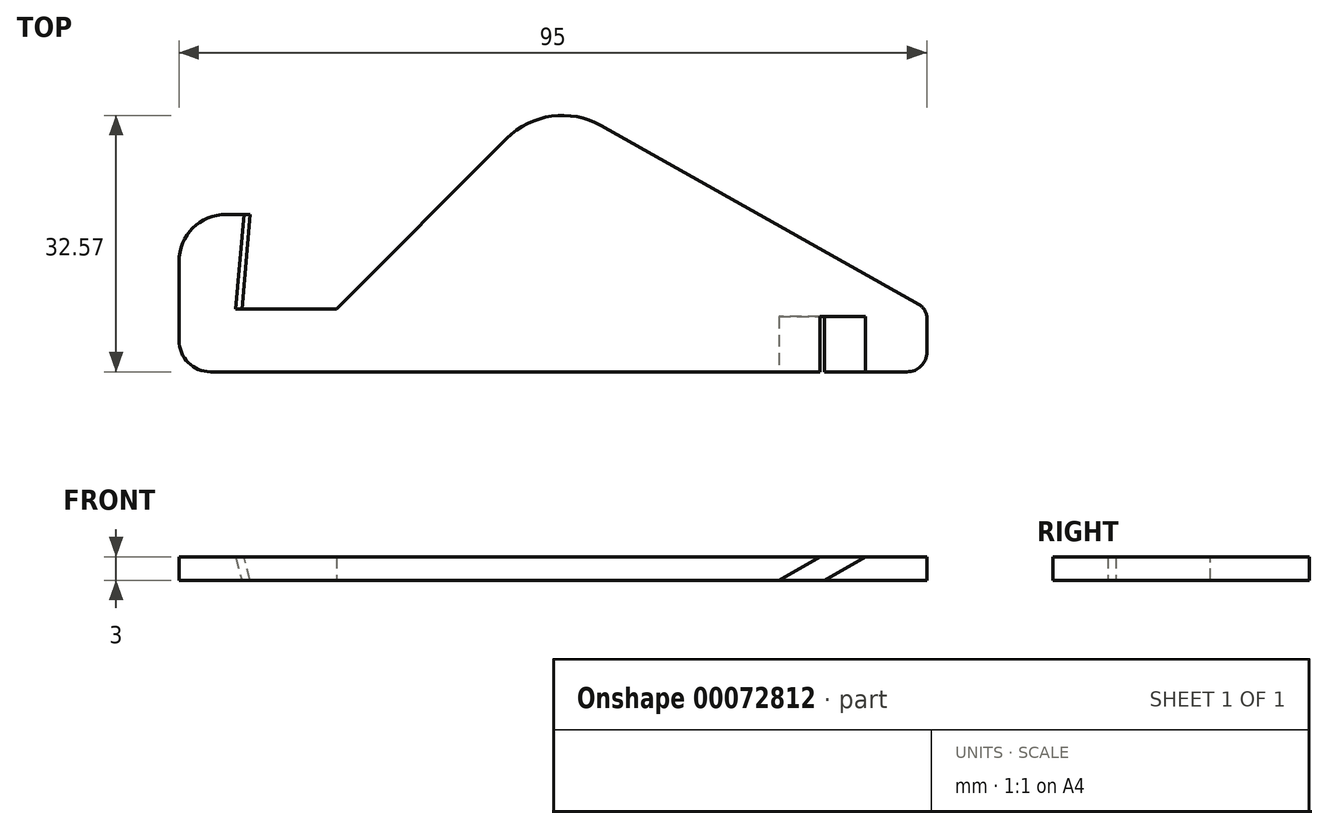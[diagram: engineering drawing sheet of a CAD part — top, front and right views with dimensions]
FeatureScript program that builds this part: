
annotation { "Feature Type Name" : "Feature", "Feature Type Description" : "" }
export const myFeature = defineFeature(function(context is Context, id is Id, definition is map)
    precondition{}
    {
        {
            var Q0;
            Q0=qCreatedBy(makeId("Top.planeOp"),FACE);
            var sketch = newSketch(context, id + "F0", { "sketchPlane" : qUnion([Q0])});
            skLineSegment(sketch, "E0.bottom", {"start": v(0, 0) * mm, "end": v(95, 0) * mm, "construction": true});
            skLineSegment(sketch, "E1", {"start": v(92.5, 0) * mm, "end": v(4, 0) * mm});
            skPoint(sketch, "E2.visualSharp", {"position": v(0, 0) * mm});
            skLineSegment(sketch, "E3", {"start": v(8, 8) * mm, "end": v(20, 8) * mm});
            skLineSegment(sketch, "E4", {"start": v(20, 8) * mm, "end": v(41.64, 29.64) * mm});
            skLineSegment(sketch, "E5", {"start": v(9.05, 20) * mm, "end": v(8, 8) * mm});
            skPoint(sketch, "E6.visualSharp", {"position": v(8, 8) * mm});
            skLineSegment(sketch, "E7", {"start": v(95, 2.5) * mm, "end": v(95, 6.83) * mm});
            skLineSegment(sketch, "E8", {"start": v(93.98, 8.57) * mm, "end": v(53.61, 31.28) * mm});
            skPoint(sketch, "E9.visualSharp", {"position": v(47, 35) * mm});
            skArc(sketch, "E9.filletArc", {"start": v(53.61, 31.28) * mm, "mid": v(47.35, 32.47) * mm, "end": v(41.64, 29.64) * mm});
            skPoint(sketch, "E10.visualSharp", {"position": v(95, 8) * mm});
            skArc(sketch, "E10.filletArc", {"start": v(95, 6.83) * mm, "mid": v(94.73, 7.84) * mm, "end": v(93.98, 8.57) * mm});
            skPoint(sketch, "E11.visualSharp", {"position": v(95, 0) * mm});
            skArc(sketch, "E11.filletArc", {"start": v(92.5, 0) * mm, "mid": v(94.27, 0.73) * mm, "end": v(95, 2.5) * mm});
            skArc(sketch, "E12.filletArc", {"start": v(0, 4) * mm, "mid": v(1.17, 1.17) * mm, "end": v(4, 0) * mm});
            skLineSegment(sketch, "E13", {"start": v(0, 4) * mm, "end": v(0, 14) * mm});
            skLineSegment(sketch, "E14", {"start": v(6, 20) * mm, "end": v(9.05, 20) * mm});
            skPoint(sketch, "E15.visualSharp", {"position": v(0, 20) * mm});
            skArc(sketch, "E15.filletArc", {"start": v(6, 20) * mm, "mid": v(1.76, 18.24) * mm, "end": v(0, 14) * mm});
            skSolve(sketch);
        }
        {
            var Q0;
            Q0=makeQuery(id+"F0.imprint","IMPRINT",FACE,{"disambiguationData":[TD([[makeQuery(id+"F0.imprint","IMPRINT",EDGE,{"derivedFrom":sQuery(id+"F0.wireOp",EDGE,"E1")}),-1.0]])]});
            extrude(context, id + "F1", {"entities" : qUnion([Q0]), "depth" : 3 * mm});
        }
        {
            var Q0;
            Q0=makeQuery(id+"F1.opExtrude","CAP_FACE",FACE,{"disambiguationData":[OSD([sQuery(id+"F0.wireOp",EDGE,"E1"),sQuery(id+"F0.wireOp",EDGE,"E3"),sQuery(id+"F0.wireOp",EDGE,"E4"),sQuery(id+"F0.wireOp",EDGE,"E5"),sQuery(id+"F0.wireOp",EDGE,"E7"),sQuery(id+"F0.wireOp",EDGE,"E8"),sQuery(id+"F0.wireOp",EDGE,"E9.filletArc"),sQuery(id+"F0.wireOp",EDGE,"E10.filletArc"),sQuery(id+"F0.wireOp",EDGE,"E11.filletArc"),sQuery(id+"F0.wireOp",EDGE,"E12.filletArc"),sQuery(id+"F0.wireOp",EDGE,"E13"),sQuery(id+"F0.wireOp",EDGE,"E14"),sQuery(id+"F0.wireOp",EDGE,"E15.filletArc")])],"isStart":true});
            var sketch = newSketch(context, id + "F2", { "sketchPlane" : qUnion([Q0])});
            skLineSegment(sketch, "E16", {"start": v(82, 0) * mm, "end": v(82, -20.57) * mm, "construction": true});
            skSolve(sketch);
        }
        {
            var Q0;
            Q0=sQuery(id+"F2.wireOp",EDGE,"E16");
            cPlane(context, id + "F3", {"entities" : qUnion([Q0]), "cplaneType" : CPlaneType.LINE_ANGLE, "offset" : 150 * mm, "angle" : 60 * degree, "width" : 150 * mm, "height" : 150 * mm});
        }
        {
            var Q0;
            Q0=qCreatedBy(id+"F3.planeOp",FACE);
            var sketch = newSketch(context, id + "F4", { "sketchPlane" : qUnion([Q0])});
            skLineSegment(sketch, "E17.0", {"start": v(0, -41) * mm, "end": v(20.57, -41) * mm, "construction": true});
            skLineSegment(sketch, "E18.bottom", {"start": v(0, -41) * mm, "end": v(7, -41) * mm});
            skLineSegment(sketch, "E18.top", {"start": v(0, -38.1) * mm, "end": v(7, -38.1) * mm});
            skLineSegment(sketch, "E18.left", {"start": v(0, -41) * mm, "end": v(0, -38.1) * mm});
            skLineSegment(sketch, "E18.right", {"start": v(7, -41) * mm, "end": v(7, -38.1) * mm});
            skSolve(sketch);
        }
        {
            var Q0;
            Q0=makeQuery(id+"F1.opExtrude","CAP_EDGE",EDGE,{"disambiguationData":[OSD([sQuery(id+"F0.wireOp",EDGE,"E5")])],"isStart":false});
            chamfer(context, id + "F5", {"entities" : qUnion([Q0]), "chamferType" : ChamferType.OFFSET_ANGLE, "width" : 3 * mm, "oppositeDirection" : false, "angle" : 15 * degree, "tangentPropagation" : true});
        }
        {
            var Q0;
            Q0=makeQuery(id+"F4.imprint","IMPRINT",FACE,{"disambiguationData":[TD([[makeQuery(id+"F4.imprint","IMPRINT",EDGE,{"derivedFrom":sQuery(id+"F4.wireOp",EDGE,"E18.bottom")}),1.0]])]});
            extrude(context, id + "F6", {"entities" : qUnion([Q0]), "operationType" : NewBodyOperationType.REMOVE, "endBound" : BoundingType.SYMMETRIC, "depth" : 25 * mm});
        }
    });
